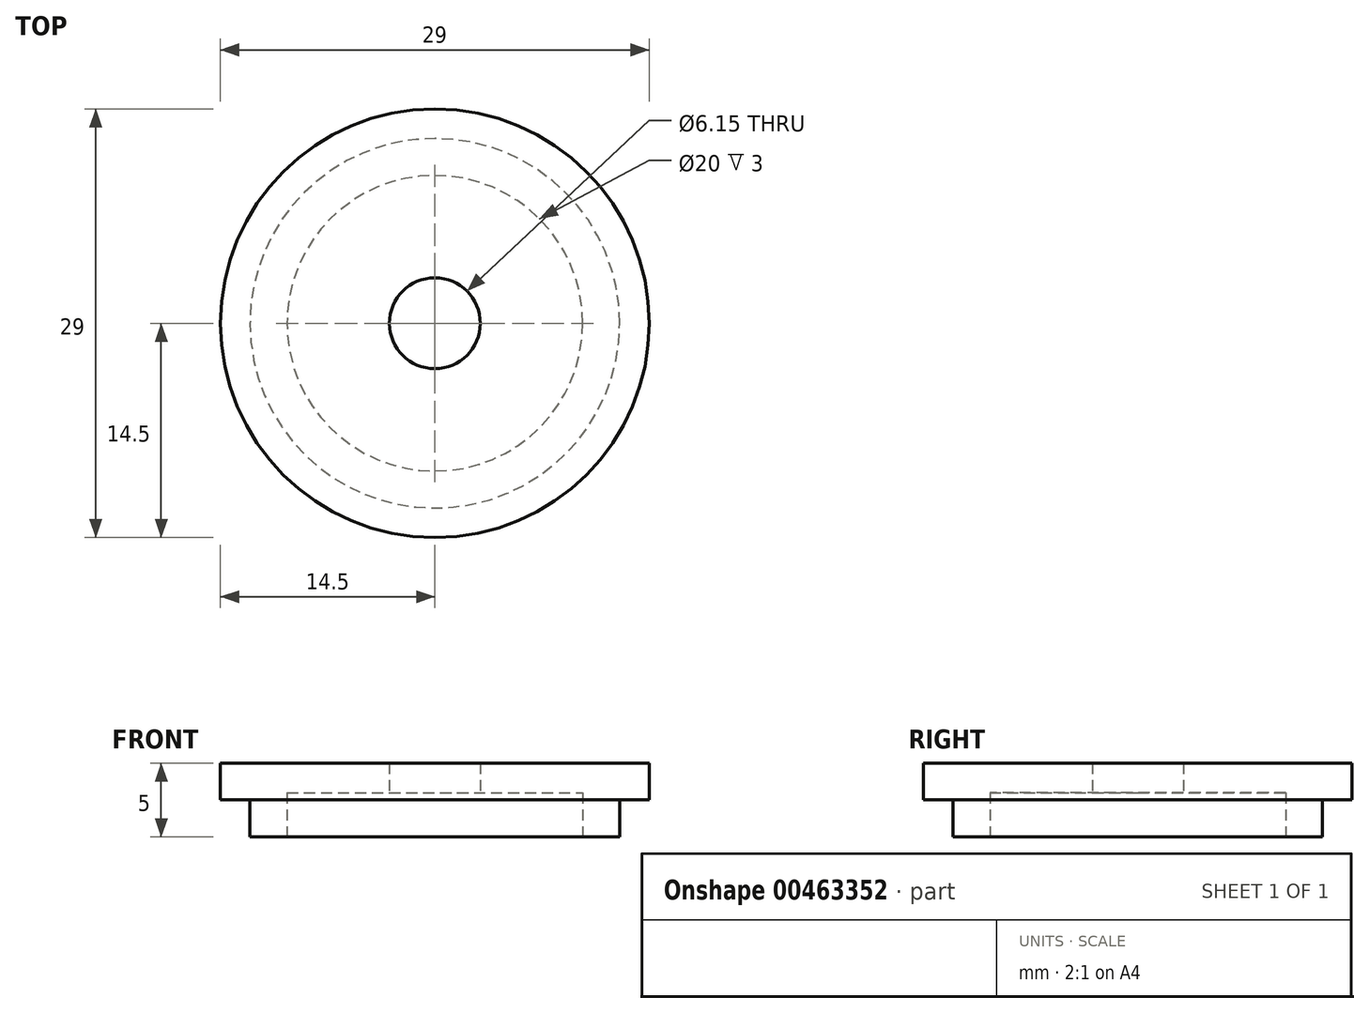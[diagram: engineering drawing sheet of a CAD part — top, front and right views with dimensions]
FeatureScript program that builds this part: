
annotation { "Feature Type Name" : "Feature", "Feature Type Description" : "" }
export const myFeature = defineFeature(function(context is Context, id is Id, definition is map)
    precondition{}
    {
        {
            var Q0;
            Q0=qCreatedBy(makeId("Front.planeOp"),FACE);
            var sketch = newSketch(context, id + "F0", { "sketchPlane" : qUnion([Q0])});
            skLineSegment(sketch, "E0", {"start": v(0, 0) * mm, "end": v(0, 5) * mm, "construction": true});
            skLineSegment(sketch, "E1.bottom", {"start": v(10, 0) * mm, "end": v(12.5, 0) * mm});
            skLineSegment(sketch, "E1.top", {"start": v(3.08, 5) * mm, "end": v(14.5, 5) * mm});
            skLineSegment(sketch, "E1.left", {"start": v(3.07, 3) * mm, "end": v(3.07, 5) * mm});
            skLineSegment(sketch, "E1.right", {"start": v(14.5, 2.5) * mm, "end": v(14.5, 5) * mm});
            skLineSegment(sketch, "E2", {"start": v(14.5, 2.5) * mm, "end": v(12.5, 2.5) * mm});
            skLineSegment(sketch, "E3", {"start": v(12.5, 2.5) * mm, "end": v(12.5, 0) * mm});
            skPoint(sketch, "E4.orphan", {"position": v(14.5, 0) * mm});
            skLineSegment(sketch, "E5", {"start": v(3.07, 3) * mm, "end": v(10, 3) * mm});
            skLineSegment(sketch, "E6", {"start": v(10, 3) * mm, "end": v(10, 0) * mm});
            skPoint(sketch, "E7.orphan", {"position": v(3.08, 0) * mm});
            skSolve(sketch);
        }
        {
            var Q0;
            Q0=makeQuery(id+"F0.imprint","IMPRINT",FACE,{"disambiguationData":[TD([[makeQuery(id+"F0.imprint","IMPRINT",EDGE,{"derivedFrom":sQuery(id+"F0.wireOp",EDGE,"E1.bottom")}),1.0]])]});
            var Q1;
            Q1=sQuery(id+"F0.wireOp",EDGE,"E0");
            revolve(context, id + "F1", {"entities" : qUnion([Q0]), "axis" : qUnion([Q1]), "revolveType" : RevolveType.FULL});
        }
    });
